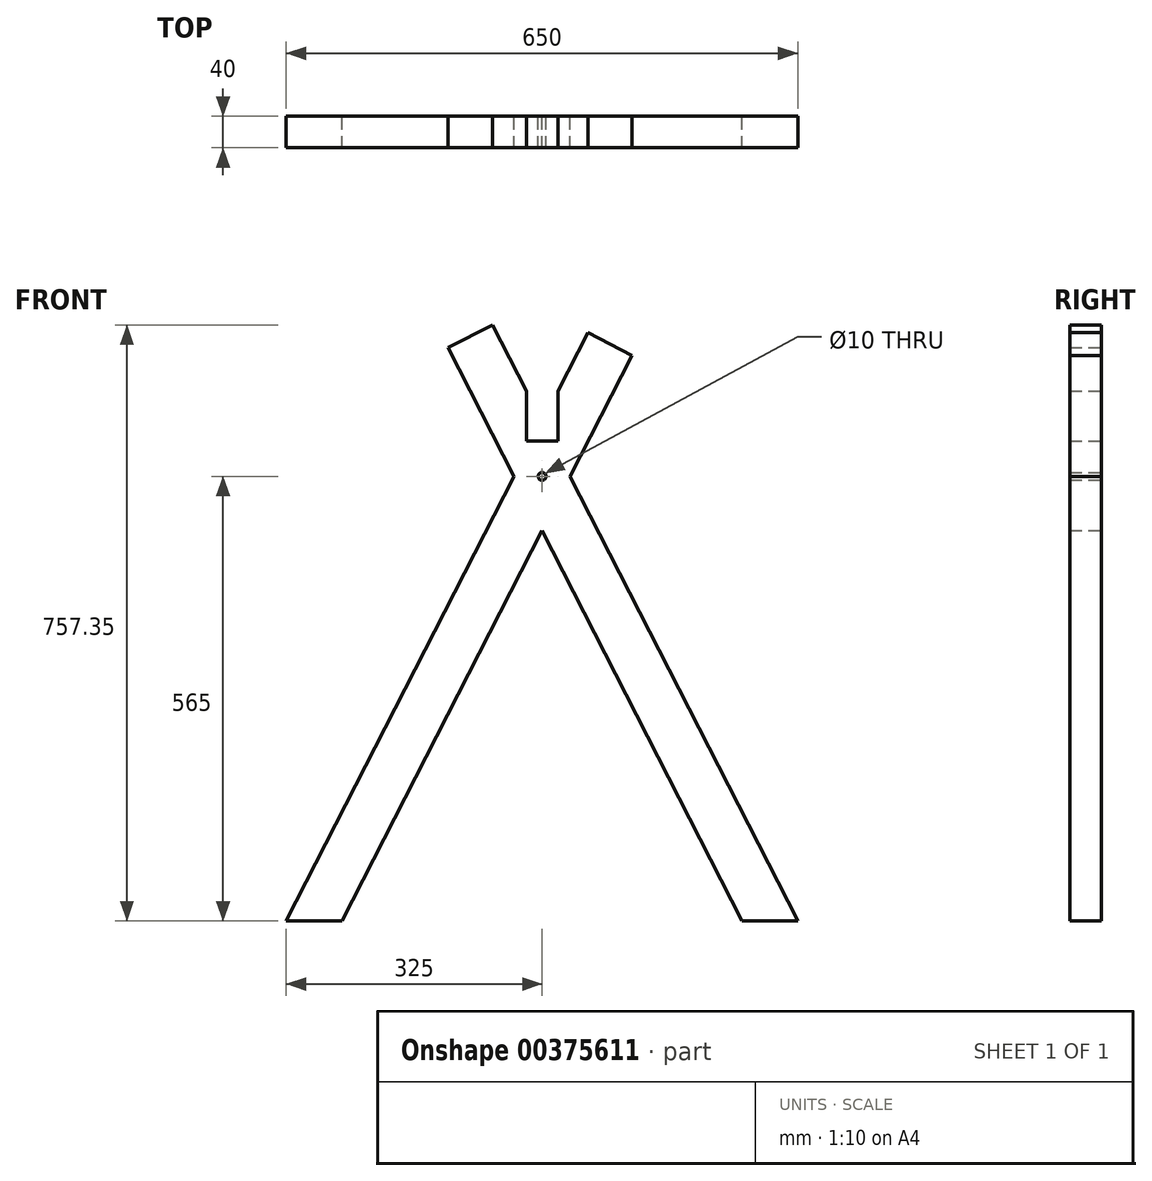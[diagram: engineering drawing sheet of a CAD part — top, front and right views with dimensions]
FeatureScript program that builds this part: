
annotation { "Feature Type Name" : "Feature", "Feature Type Description" : "" }
export const myFeature = defineFeature(function(context is Context, id is Id, definition is map)
    precondition{}
    {
        {
            var Q0;
            Q0=qCreatedBy(makeId("Front.planeOp"),FACE);
            var sketch = newSketch(context, id + "F0", { "sketchPlane" : qUnion([Q0])});
            skLineSegment(sketch, "E0", {"start": v(-254.2, -650) * mm, "end": v(254.2, -650) * mm, "construction": true});
            skPoint(sketch, "E1", {"position": v(0, -650) * mm});
            skLineSegment(sketch, "E2.bottom", {"start": v(-63.2, 107.35) * mm, "end": v(-20, 23.08) * mm});
            skLineSegment(sketch, "E2.top", {"start": v(-119.26, 78.61) * mm, "end": v(254.2, -650) * mm});
            skLineSegment(sketch, "E2.left", {"start": v(-63.2, 107.35) * mm, "end": v(-119.26, 78.61) * mm});
            skLineSegment(sketch, "E3.bottom", {"start": v(-325, -650) * mm, "end": v(-12.33, -40) * mm});
            skLineSegment(sketch, "E3.top", {"start": v(-254.2, -650) * mm, "end": v(114.14, 68.63) * mm});
            skLineSegment(sketch, "E3.right", {"start": v(58.08, 97.37) * mm, "end": v(114.14, 68.63) * mm});
            skLineSegment(sketch, "E4", {"start": v(254.2, -650) * mm, "end": v(325, -650) * mm});
            skLineSegment(sketch, "E5", {"start": v(-254.2, -650) * mm, "end": v(-325, -650) * mm});
            skPoint(sketch, "E6", {"position": v(-35.4, -85) * mm});
            skPoint(sketch, "E7", {"position": v(35.4, -85) * mm});
            skLineSegment(sketch, "E8", {"start": v(-35.4, -85) * mm, "end": v(35.4, -85) * mm, "construction": true});
            skCircle(sketch, "E9", {"center": v(0, -85) * mm, "radius": 5 * mm});
            skLineSegment(sketch, "E10.bottom", {"start": v(20, -40) * mm, "end": v(-20, -40) * mm});
            skLineSegment(sketch, "E10.top", {"start": v(20, 40) * mm, "end": v(-20, 40) * mm, "construction": true});
            skLineSegment(sketch, "E10.left", {"start": v(20, -40) * mm, "end": v(20, 40) * mm});
            skLineSegment(sketch, "E10.right", {"start": v(-20, -40) * mm, "end": v(-20, 40) * mm});
            skPoint(sketch, "E10.middle", {"position": v(0, 0) * mm});
            skLineSegment(sketch, "E11.trimOffspring", {"start": v(20, 23.08) * mm, "end": v(58.08, 97.37) * mm});
            skLineSegment(sketch, "E12.trimOffspring", {"start": v(12.33, -40) * mm, "end": v(325, -650) * mm});
            skSolve(sketch);
        }
        {
            var Q0;
            Q0 = qSketchRegion(id + "F0", true);
            extrude(context, id + "F1", {"entities" : qUnion([Q0]), "depth" : 40 * mm});
        }
    });
